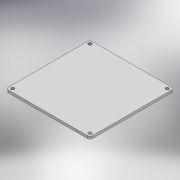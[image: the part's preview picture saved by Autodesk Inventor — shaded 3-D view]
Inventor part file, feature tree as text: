
AUTODESK INVENTOR PART (.ipt)
format: ipt  version: 2017 (Build 210142000, 142)  size: 116,224 bytes
history: native  units: mm
features: extrude x1, sketch x1
ambient origin geometry x8: Origin, YZ Plane, XZ Plane, XY Plane, X Axis, Y Axis, Z Axis, Center Point
bodies: Body1 (feature_tree)
feature tree (2):
  extrude  "Extrusion2"  Depth=100.0mm
  sketch  "Sketch1"  dims[d0=100.0mm d1=100.0mm d4=4.0mm d5=3.0mm d6=4.0mm d7=3.0mm d8=0.0mm]
